# Revit family: Lavatory-TOTO-Transitional-Prominence-LHT242(G)
name_source: partatom
category: Plumbing Fixtures
revit_build: Autodesk Revit Architecture 2013 (Build: 20130531_2115(x64)
units: mm (PartAtom-declared; Revit-internal decimal feet)

## types (2) — shared parameters
04 CSI = 22 42 16
95 CSI = 15410
ADA Compliant = No
Assembly Code = D2010310
Basin Depth = 1' - 2 3/4"
Basin Width = 1' - 11 1/8"
Certifications = IAPMO(cUPC), State of Massachusetts and others
Code Compliance = UPC, IPC, NSPC, NPC Canada, and others
Cold Water Connection Radius = 0' - 0 3/16"
Cold Water Connector = Cold Water Connection
Color Availability = #01 Cotton, #03 Bone, #11 Colonial White, #12 Sedona Beige, #51 Ebony (not available in SanaGloss)
Default Elevation = 0' - 0"
Depth = 1' - 9 1/2"
Finish = Vitreous China - TOTO - 01 Cotton
Height = 1' - 11 5/16"
Hot Water Connection Radius = 0' - 0 3/16"
Hot Water Connector = Hot Water Connection
Industry Standards = Meets and exceeds ASME A112.19.2/CSA B45.1
Manufacturer = TOTO USA, Inc.
Manufacturer Fax = (770) 282-0002
Material = Vitreous china lavatory and  shroud
Model = LHT242
Sanitary Connector = Sanitary Connection
Series = Prominence
Shipping Weight = 46.00 lb
Spec Sheet URL = http://assets.totousa.com
Style = Transitional
Subcategory = Lavatories
Toto BIM Number = BM-00328
URL = http://www.totousa.com
Warranty = One Year Limited Warranty
Warranty URL = http://www.totousa.com
Waste Connection NPT Radius = 0' - 0 5/8"
Width = 2' - 2"

## per-type parameters (varying)
| type | Description | SanaGloss |
| LHT242 | Prominence® Wall Mount Lavatory | No |
| LHT242G | Prominence® Wall Mount Lavatory - with SanaGloss | Yes |

## geometry (parser evidence)
native form markers: Blend x6, Sweep x4
no freeform markers — native parametric forms only
